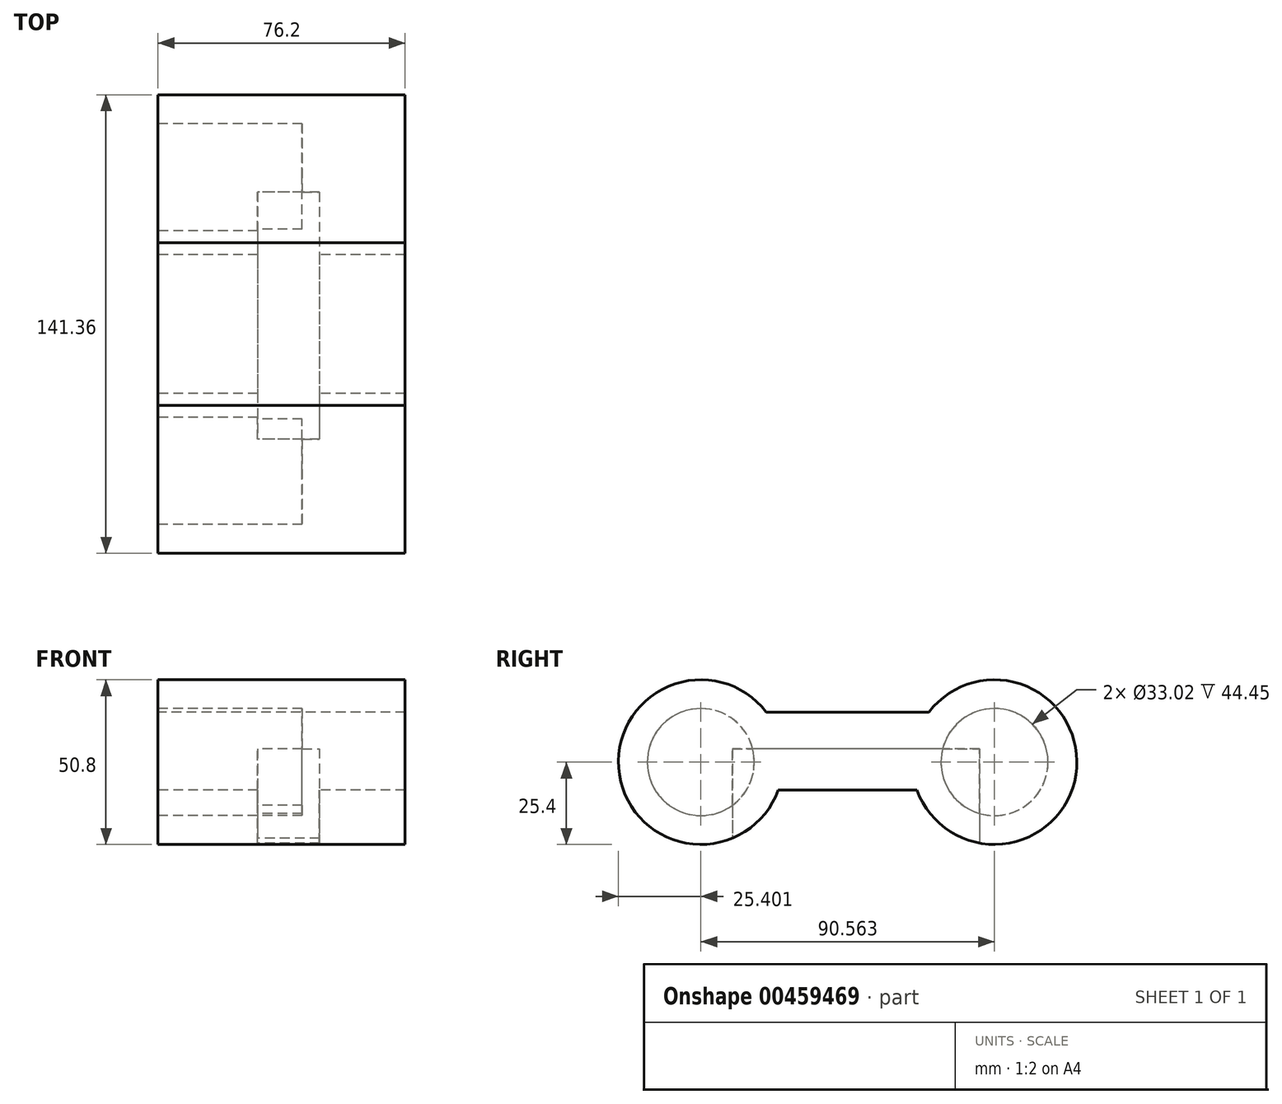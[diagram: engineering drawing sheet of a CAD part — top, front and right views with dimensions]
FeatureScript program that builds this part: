
annotation { "Feature Type Name" : "Feature", "Feature Type Description" : "" }
export const myFeature = defineFeature(function(context is Context, id is Id, definition is map)
    precondition{}
    {
        {
            var Q0;
            Q0=qCreatedBy(makeId("Right.planeOp"),FACE);
            var sketch = newSketch(context, id + "F0", { "sketchPlane" : qUnion([Q0])});
            skArc(sketch, "E0", {"start": v(-27.69, 15.44) * mm, "mid": v(-72.96, -3.9) * mm, "end": v(-23.96, -8.6) * mm});
            skArc(sketch, "E1", {"start": v(18.8, -8.6) * mm, "mid": v(67.8, -3.9) * mm, "end": v(22.54, 15.44) * mm});
            skLineSegment(sketch, "E2.bottom", {"start": v(-27.69, 15.44) * mm, "end": v(22.54, 15.44) * mm});
            skLineSegment(sketch, "E2.top", {"start": v(-23.96, -8.6) * mm, "end": v(18.8, -8.6) * mm});
            skPoint(sketch, "E3.orphan", {"position": v(42.7, -8.6) * mm});
            skSolve(sketch);
        }
        {
            var Q0;
            Q0 = qSketchRegion(id + "F0", true);
            extrude(context, id + "F1", {"entities" : qUnion([Q0]), "depth" : 76.2 * mm});
        }
        {
            var Q0;
            Q0=makeQuery(id+"F1.opExtrude","SWEPT_FACE",FACE,{"disambiguationData":[OSD([sQuery(id+"F0.wireOp",EDGE,"E2.top")])]});
            var sketch = newSketch(context, id + "F2", { "sketchPlane" : qUnion([Q0])});
            skLineSegment(sketch, "E4.bottom", {"start": v(30.73, -38.1) * mm, "end": v(49.78, -38.1) * mm});
            skLineSegment(sketch, "E4.top", {"start": v(30.73, 38.1) * mm, "end": v(49.78, 38.1) * mm});
            skLineSegment(sketch, "E4.left", {"start": v(30.73, -38.1) * mm, "end": v(30.73, 38.1) * mm});
            skLineSegment(sketch, "E4.right", {"start": v(49.78, -38.1) * mm, "end": v(49.78, 38.1) * mm});
            skSolve(sketch);
        }
        {
            var Q0;
            Q0 = qSketchRegion(id + "F2", true);
            extrude(context, id + "F3", {"entities" : qUnion([Q0]), "operationType" : NewBodyOperationType.ADD, "depth" : 25.4 * mm});
        }
        {
            var Q0;
            Q0=makeQuery(id+"F3.opExtrude","CAP_FACE",FACE,{"disambiguationData":[OSD([sQuery(id+"F2.wireOp",EDGE,"E4.bottom"),sQuery(id+"F2.wireOp",EDGE,"E4.top"),sQuery(id+"F2.wireOp",EDGE,"E4.left"),sQuery(id+"F2.wireOp",EDGE,"E4.right")])],"isStart":false});
            extrude(context, id + "F4", {"entities" : qUnion([Q0]), "operationType" : NewBodyOperationType.REMOVE, "oppositeDirection" : true, "depth" : 38.1 * mm});
        }
        {
            var Q0;
            Q0=makeQuery(id+"F1.opExtrude","CAP_FACE",FACE,{"disambiguationData":[OSD([sQuery(id+"F0.wireOp",EDGE,"E0"),sQuery(id+"F0.wireOp",EDGE,"E1"),sQuery(id+"F0.wireOp",EDGE,"E2.bottom"),sQuery(id+"F0.wireOp",EDGE,"E2.top")])],"isStart":true});
            var sketch = newSketch(context, id + "F5", { "sketchPlane" : qUnion([Q0])});
            skCircle(sketch, "E5", {"center": v(47.86, 0) * mm, "radius": 16.51 * mm});
            skCircle(sketch, "E6", {"center": v(-42.7, 0) * mm, "radius": 16.51 * mm});
            skSolve(sketch);
        }
        {
            var Q0;
            Q0=makeQuery(id+"F5.imprint","IMPRINT",FACE,{"disambiguationData":[TD([[makeQuery(id+"F5.imprint","IMPRINT",EDGE,{"derivedFrom":sQuery(id+"F5.wireOp",EDGE,"E6")}),1.0]])]});
            var Q1;
            Q1=makeQuery(id+"F5.imprint","IMPRINT",FACE,{"disambiguationData":[TD([[makeQuery(id+"F5.imprint","IMPRINT",EDGE,{"derivedFrom":sQuery(id+"F5.wireOp",EDGE,"E5")}),1.0]])]});
            extrude(context, id + "F6", {"entities" : qUnion([Q0, Q1]), "operationType" : NewBodyOperationType.REMOVE, "oppositeDirection" : true, "depth" : 44.45 * mm});
        }
    });
